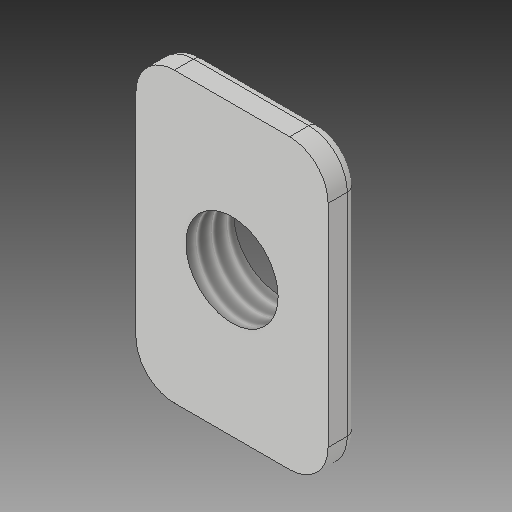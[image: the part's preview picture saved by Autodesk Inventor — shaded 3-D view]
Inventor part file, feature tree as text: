
AUTODESK INVENTOR PART (.ipt)
format: ipt  version: 2017 (Build 210142000, 142)  size: 157,696 bytes
history: native  units: mm
features: other x3, sketch x2
ambient origin geometry x8: Origin, YZ Plane, XZ Plane, XY Plane, X Axis, Y Axis, Z Axis, Center Point
bodies: Solid1 (feature_tree)
feature tree (5):
  other  "M5 Tee Nut-Generic.ipt"
  other  "Solid1::M5 Tee Nut-Generic.ipt"
  other  "TaggingFeature1"
  sketch  "Sketch1"  dims[d0=10.0mm]
  sketch  "Sketch2"
